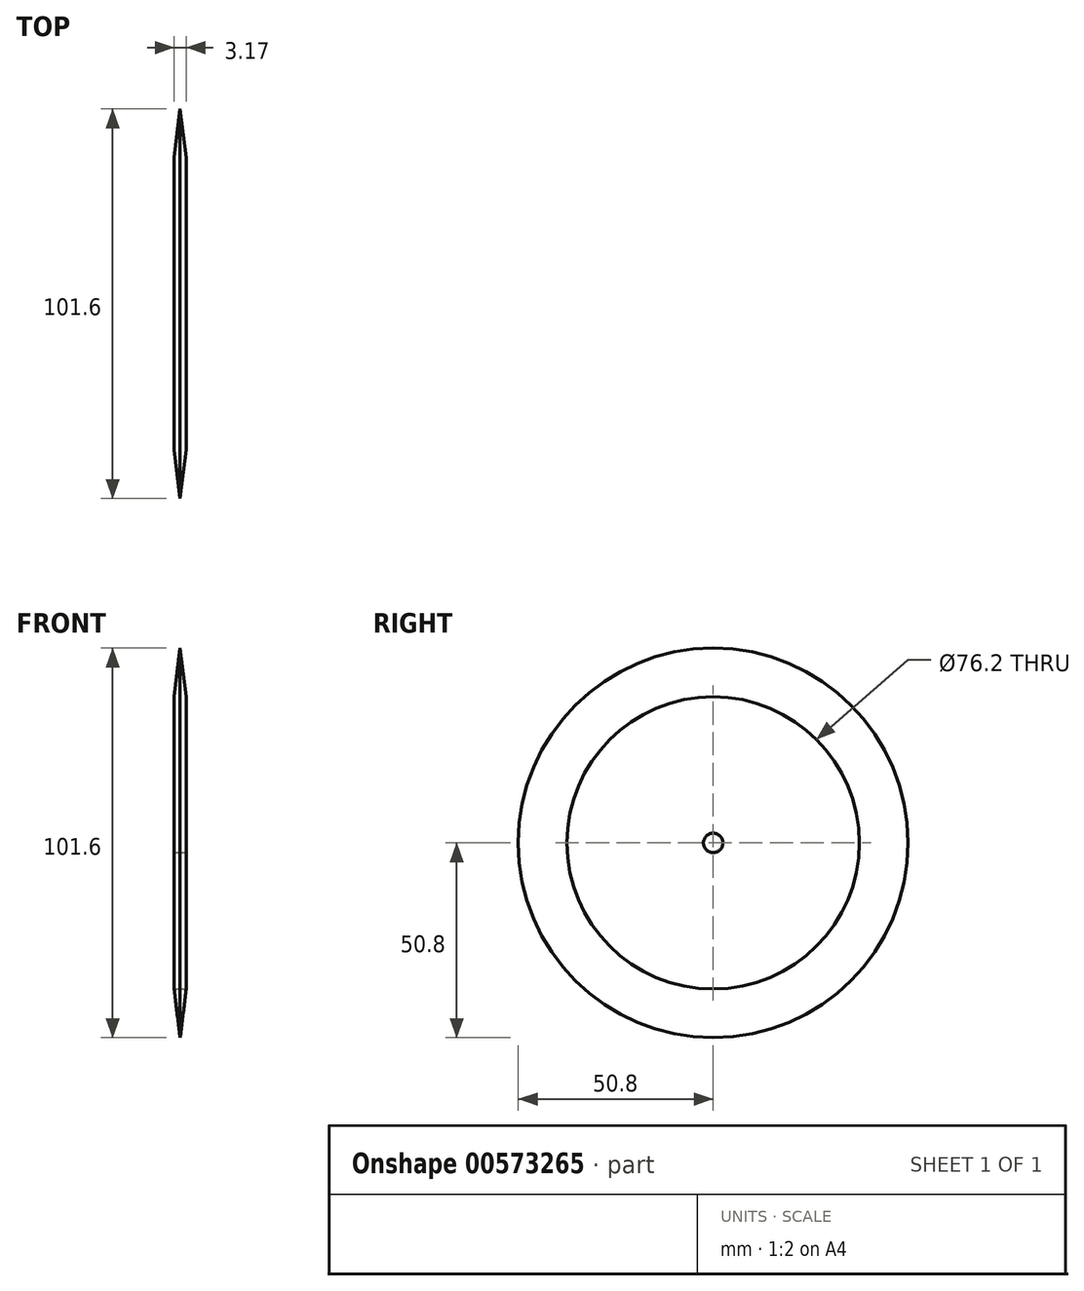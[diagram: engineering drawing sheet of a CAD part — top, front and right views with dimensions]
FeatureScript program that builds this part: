
annotation { "Feature Type Name" : "Feature", "Feature Type Description" : "" }
export const myFeature = defineFeature(function(context is Context, id is Id, definition is map)
    precondition{}
    {
        {
            var Q0;
            Q0=qCreatedBy(makeId("Front.planeOp"),FACE);
            var sketch = newSketch(context, id + "F0", { "sketchPlane" : qUnion([Q0])});
            skLineSegment(sketch, "E0", {"start": v(5.68, 0) * mm, "end": v(8.85, 0) * mm});
            skLineSegment(sketch, "E1.left", {"start": v(5.68, 0) * mm, "end": v(5.68, 0) * mm});
            skLineSegment(sketch, "E1.right", {"start": v(8.85, 0) * mm, "end": v(8.85, 0) * mm});
            skLineSegment(sketch, "E2.bottom", {"start": v(8.85, -38.1) * mm, "end": v(5.68, -38.1) * mm});
            skLineSegment(sketch, "E2.top", {"start": v(8.85, 0) * mm, "end": v(5.68, 0) * mm});
            skLineSegment(sketch, "E2.left", {"start": v(8.85, -38.1) * mm, "end": v(8.85, 0) * mm});
            skLineSegment(sketch, "E2.right", {"start": v(5.68, -38.1) * mm, "end": v(5.68, 0) * mm});
            skLineSegment(sketch, "E3.bottom", {"start": v(5.68, 38.1) * mm, "end": v(8.85, 38.1) * mm});
            skLineSegment(sketch, "E3.left", {"start": v(5.68, 38.1) * mm, "end": v(5.68, 0) * mm});
            skLineSegment(sketch, "E3.right", {"start": v(8.85, 38.1) * mm, "end": v(8.85, 0) * mm});
            skLineSegment(sketch, "E4.bottom", {"start": v(4.85, 33.61) * mm, "end": v(7.27, 38.1) * mm});
            skLineSegment(sketch, "E5", {"start": v(7.27, 38.1) * mm, "end": v(-3.92, 44.11) * mm});
            skLineSegment(sketch, "E6", {"start": v(-3.92, 44.11) * mm, "end": v(5.68, 38.1) * mm});
            skLineSegment(sketch, "E7", {"start": v(8.85, 38.1) * mm, "end": v(-3.92, 44.11) * mm});
            skLineSegment(sketch, "E8", {"start": v(7.27, -38.1) * mm, "end": v(7.27, -50.8) * mm});
            skLineSegment(sketch, "E9", {"start": v(7.27, -50.8) * mm, "end": v(5.68, -38.1) * mm});
            skLineSegment(sketch, "E10", {"start": v(8.85, -38.1) * mm, "end": v(7.27, -50.8) * mm});
            skLineSegment(sketch, "E11.top", {"start": v(8.85, 2.54) * mm, "end": v(5.68, 2.54) * mm});
            skLineSegment(sketch, "E11.left", {"start": v(8.85, 0) * mm, "end": v(8.85, 2.54) * mm});
            skLineSegment(sketch, "E11.right", {"start": v(5.68, 0) * mm, "end": v(5.68, 2.54) * mm});
            skLineSegment(sketch, "E12.top", {"start": v(5.68, -2.54) * mm, "end": v(8.85, -2.54) * mm});
            skLineSegment(sketch, "E12.left", {"start": v(5.68, 0) * mm, "end": v(5.68, -2.54) * mm});
            skLineSegment(sketch, "E12.right", {"start": v(8.85, 0) * mm, "end": v(8.85, -2.54) * mm});
            skSolve(sketch);
        }
        {
            var Q0;
            {var subQ1=sQuery(id+"F0.wireOp",EDGE,"E2.left");Q0=makeQuery(id+"F0.imprint","IMPRINT",FACE,{"disambiguationData":[TD([[makeQuery(id+"F0.imprint","IMPRINT",EDGE,{"derivedFrom":subQ1}),1.0]])]});}
            var Q1;
            {var subQ2=sQuery(id+"F0.wireOp",EDGE,"E8");Q1=makeQuery(id+"F0.imprint","IMPRINT",FACE,{"disambiguationData":[TD([[makeQuery(id+"F0.imprint","IMPRINT",EDGE,{"derivedFrom":subQ2}),1.0]])]});}
            var Q2;
            {var subQ2=sQuery(id+"F0.wireOp",EDGE,"E8");Q2=makeQuery(id+"F0.imprint","IMPRINT",FACE,{"disambiguationData":[TD([[makeQuery(id+"F0.imprint","IMPRINT",EDGE,{"derivedFrom":subQ2}),-1.0]])]});}
            var Q3;
            Q3=sQuery(id+"F0.wireOp",EDGE,"E2.top");
            revolve(context, id + "F1", {"entities" : qUnion([Q0, Q1, Q2]), "axis" : qUnion([Q3]), "revolveType" : RevolveType.FULL});
        }
    });
